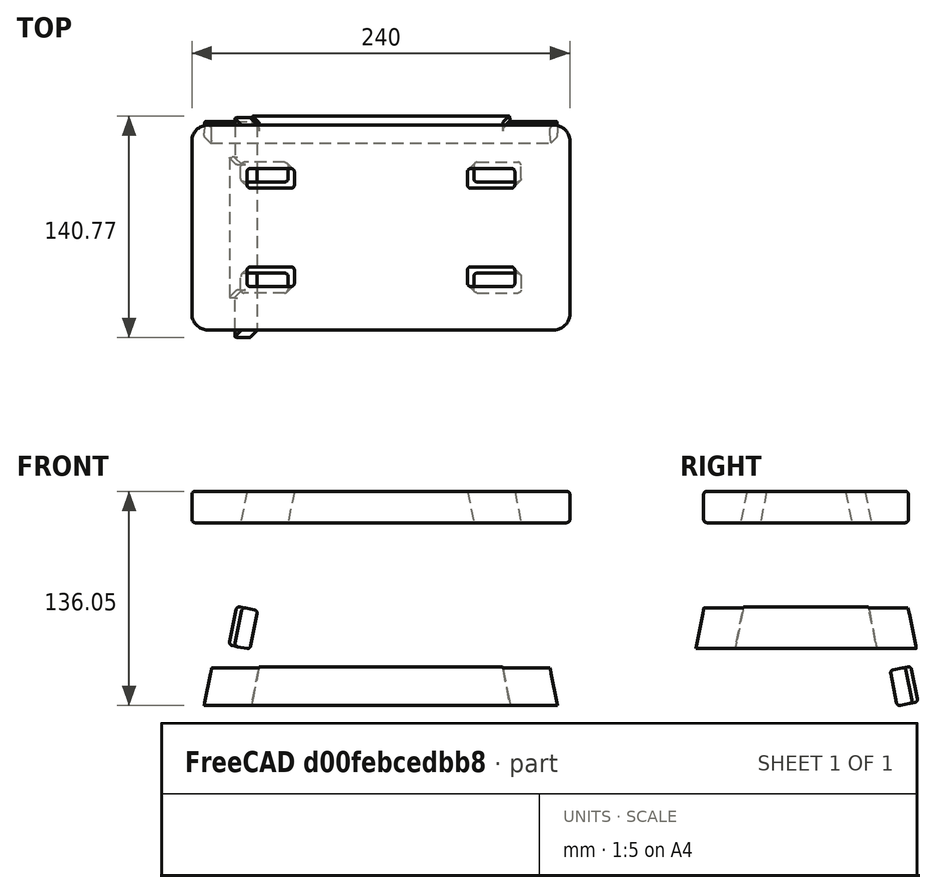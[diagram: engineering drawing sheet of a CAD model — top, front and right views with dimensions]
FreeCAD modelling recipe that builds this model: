
FCSTD DOCUMENT  (FreeCAD 1.0R39109 (Git))
Label: Chair full
License: All rights reserved
LicenseURL: https://en.wikipedia.org/wiki/All_rights_reserved
objects: Part::Cut×6, Part::Mirroring×5, Part::Feature×4, App::Part×1
note: 15 computed .brp shape members not serialized (recipe doc carries the construction recipe); baked Part::Feature solids carry a one-line shape summary decoded from their .brp

FEATURE [Part::Feature] Part__Feature  label="Fillet002"
  shape: bbox 241.6 x 131.6 x 20 mm, 26 faces (baked)
FEATURE [Part::Feature] Part__Feature001  label="Fillet003"
  shape: bbox 70.06 x 65.06 x 201.6 mm, 14 faces (baked)
FEATURE [Part::Feature] Part__Feature002  label="Fillet"
  Placement = pos=(0,0,0) rot=(0.57735,0.57735,0.57735;2.0944rad)
  shape: bbox 224.4 x 17.04 x 24.49 mm, 18 faces (baked)
FEATURE [Part::Feature] Part__Feature003  label="Fillet001"
  Placement = pos=(0,0,0) rot=(1,0,0;1.5708rad)
  shape: bbox 17.43 x 140 x 26.46 mm, 18 faces (baked)
FEATURE [Part::Cut] Cut
  Base = -> Part__Feature001
  Refine = true
  Tool = -> Part__Feature002
FEATURE [Part::Cut] Cut001
  Base = -> Cut
  Refine = true
  Tool = -> Part__Feature003
FEATURE [Part::Mirroring] Part__Mirroring  label="Cut001 (Mirror #1)"
  Base = (0,0,0)
  Normal = (0,1,0)
  Source = -> Cut001
FEATURE [Part::Mirroring] Part__Mirroring001  label="Cut001 (Mirror #2)"
  Base = (0,0,0)
  Normal = (1,0,0)
  Source = -> Part__Mirroring
FEATURE [Part::Mirroring] Part__Mirroring002  label="Cut001 (Mirror #3)"
  Base = (0,0,0)
  Normal = (0,1,0)
  Source = -> Part__Mirroring001
FEATURE [Part::Cut] Cut002
  Base = -> Part__Feature
  Refine = true
  Tool = -> Part__Mirroring002
FEATURE [Part::Cut] Cut003
  Base = -> Cut002
  Refine = true
  Tool = -> Part__Mirroring001
FEATURE [Part::Cut] Cut004
  Base = -> Cut003
  Refine = true
  Tool = -> Part__Mirroring
FEATURE [Part::Cut] Cut005
  Base = -> Cut004
  Refine = true
  Tool = -> Cut001
FEATURE [App::Part] chair
  Group = -> [Cut003,Cut002,Part__Mirroring002,Part__Feature,Cut,Part__Mirroring001,Part__Mirroring,Cut004,Part__Feature001,Cut001,Part__Feature002,Part__Feature003,Cut005]
  Origin = -> Origin
FEATURE [Part::Mirroring] Part__Mirroring003  label="Fillet (Mirror #4)"
  Base = (0,0,0)
  Normal = (0,1,0)
  Source = -> Part__Feature002
FEATURE [Part::Mirroring] Part__Mirroring004  label="Fillet001 (Mirror #5)"
  Base = (0,0,0)
  Normal = (1,0,0)
  Source = -> Part__Feature003
